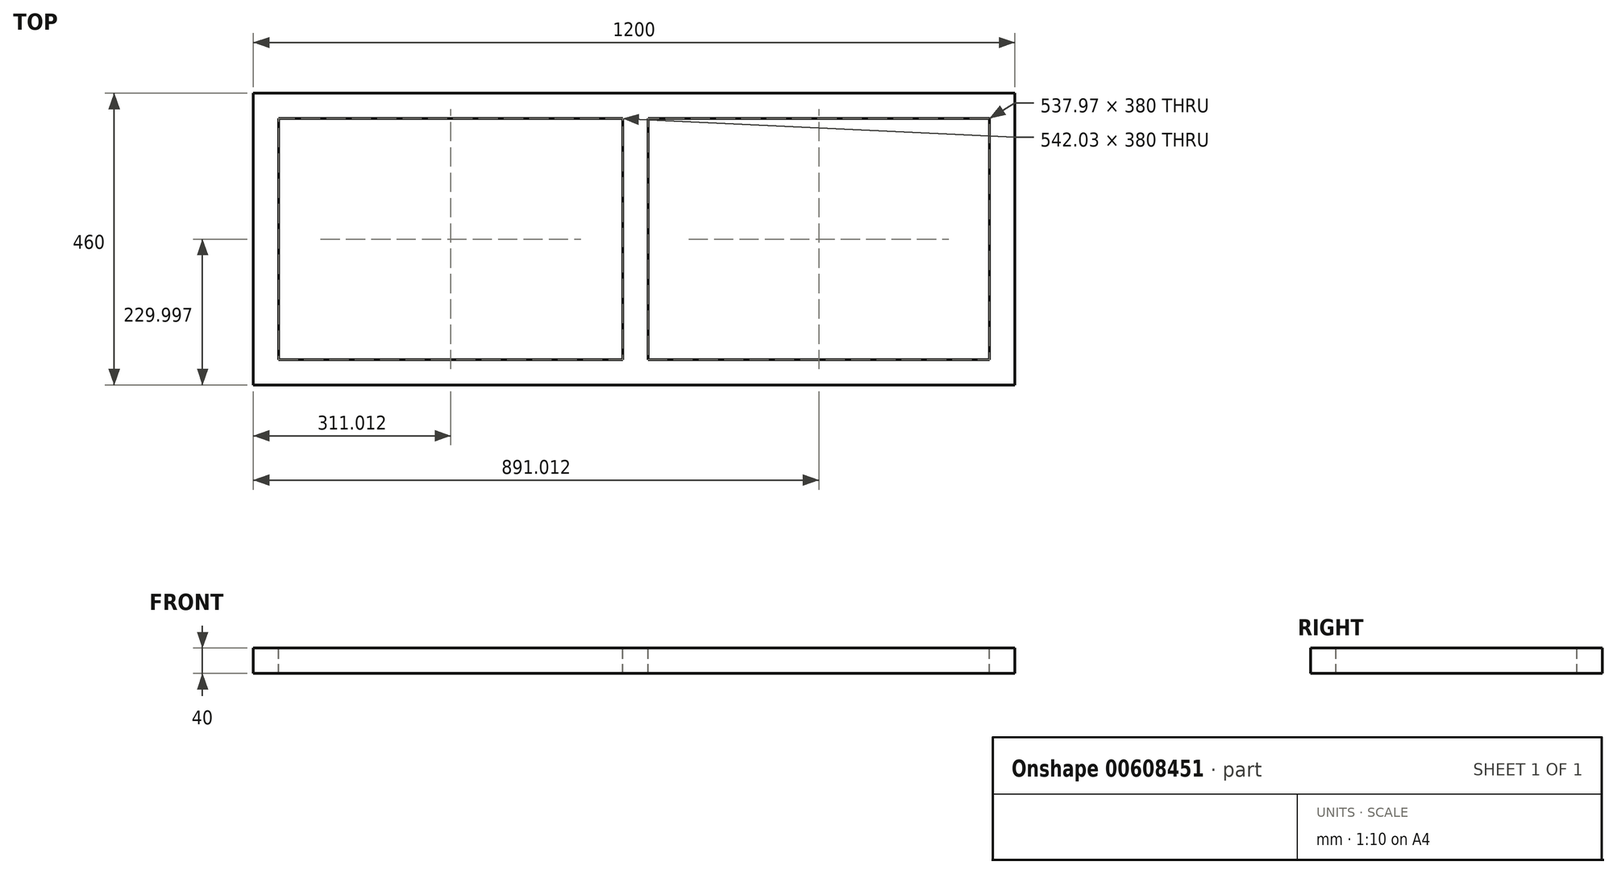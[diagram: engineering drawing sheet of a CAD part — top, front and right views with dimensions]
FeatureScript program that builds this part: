
annotation { "Feature Type Name" : "Feature", "Feature Type Description" : "" }
export const myFeature = defineFeature(function(context is Context, id is Id, definition is map)
    precondition{}
    {
        {
            var Q0;
            Q0=qCreatedBy(makeId("Top.planeOp"),FACE);
            var sketch = newSketch(context, id + "F0", { "sketchPlane" : qUnion([Q0])});
            skLineSegment(sketch, "E0.bottom", {"start": v(-998.67, -102.41) * mm, "end": v(201.33, -102.41) * mm});
            skLineSegment(sketch, "E0.top", {"start": v(-998.67, -562.41) * mm, "end": v(201.33, -562.41) * mm});
            skLineSegment(sketch, "E0.left", {"start": v(-998.67, -102.41) * mm, "end": v(-998.67, -562.41) * mm});
            skLineSegment(sketch, "E0.right", {"start": v(201.33, -102.41) * mm, "end": v(201.33, -562.41) * mm});
            skSolve(sketch);
        }
        {
            var Q0;
            Q0 = qSketchRegion(id + "F0", true);
            extrude(context, id + "F1", {"entities" : qUnion([Q0]), "depth" : 40 * mm, "offsetDistance" : 25 * mm});
        }
        {
            var Q0;
            Q0=makeQuery(id+"F1.opExtrude","CAP_FACE",FACE,{"disambiguationData":[OSD([sQuery(id+"F0.wireOp",EDGE,"E0.bottom"),sQuery(id+"F0.wireOp",EDGE,"E0.top"),sQuery(id+"F0.wireOp",EDGE,"E0.left"),sQuery(id+"F0.wireOp",EDGE,"E0.right")])],"isStart":false});
            var sketch = newSketch(context, id + "F2", { "sketchPlane" : qUnion([Q0])});
            skLineSegment(sketch, "E1.bottom", {"start": v(-958.67, -142.41) * mm, "end": v(-416.64, -142.41) * mm});
            skLineSegment(sketch, "E1.top", {"start": v(-958.67, -522.41) * mm, "end": v(-416.64, -522.41) * mm});
            skLineSegment(sketch, "E1.left", {"start": v(-958.67, -142.41) * mm, "end": v(-958.67, -522.41) * mm});
            skLineSegment(sketch, "E1.right", {"start": v(161.33, -142.41) * mm, "end": v(161.33, -522.41) * mm});
            skLineSegment(sketch, "E2", {"start": v(-416.64, -142.41) * mm, "end": v(-416.64, -522.41) * mm});
            skLineSegment(sketch, "E3", {"start": v(-376.64, -522.41) * mm, "end": v(-376.64, -142.41) * mm});
            skLineSegment(sketch, "E4.trimOffspring", {"start": v(-376.64, -142.41) * mm, "end": v(161.33, -142.41) * mm});
            skLineSegment(sketch, "E5.trimOffspring", {"start": v(-376.64, -522.41) * mm, "end": v(161.33, -522.41) * mm});
            skSolve(sketch);
        }
        {
            var Q0;
            Q0=makeQuery(id+"F2.imprint","IMPRINT",FACE,{"disambiguationData":[TD([[makeQuery(id+"F2.imprint","IMPRINT",EDGE,{"derivedFrom":sQuery(id+"F2.wireOp",EDGE,"E1.bottom")}),-1.0]])]});
            var Q1;
            Q1=makeQuery(id+"F2.imprint","IMPRINT",FACE,{"disambiguationData":[TD([[makeQuery(id+"F2.imprint","IMPRINT",EDGE,{"derivedFrom":sQuery(id+"F2.wireOp",EDGE,"E1.right")}),-1.0]])]});
            extrude(context, id + "F3", {"entities" : qUnion([Q0, Q1]), "operationType" : NewBodyOperationType.REMOVE, "endBound" : BoundingType.THROUGH_ALL, "oppositeDirection" : true, "depth" : 25 * mm, "offsetDistance" : 25 * mm});
        }
    });
